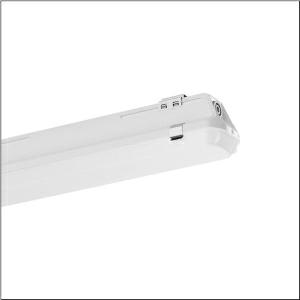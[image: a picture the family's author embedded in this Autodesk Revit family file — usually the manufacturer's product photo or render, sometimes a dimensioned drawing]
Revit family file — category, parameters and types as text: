
# Revit family: monsun_r__21_51fb10dp460b_c90e
name_source: partatom
category: Lighting Fixtures
units: mm (PartAtom-declared; Revit-internal decimal feet)

## family parameters
Cut with Voids When Loaded = No
Host = Face
Light Source = No
Part Type = Normal
Room Calculation Point = No
Round Connector Dimension = Use Diameter
Shared = No

## types (1)
- --- (1 x LED, 6060 lm, 39.4 W, 4000K)
    Apparent Load = 39 VA
    CIE Flux Codes = 47 77 93 94 100
    Color Rendering = 80
    Color Temperature = 4000K
    Default Elevation = 1800 mm
    Description = Monsun® 21, damp-proof luminaire, chain hanger, primary optical cover: enclosure, of PMMA, light emission: direct distribution, primary light characteristic: symmetric, installation type: suspended mounting, surface-mounted, horizontal mounting, vertical mounting, LED, rated luminous flux: 6.060lm, luminous efficacy: 154lm/W, light colour: 840, colour temperature: 4000K, control gear: ECG DALI, with terminal, 5-pole, max. 2.5mm², mains connection: 220..240V, AC, 50/60Hz, rated input power: 39W, housing, of glass-fibre reinforced polyester, uncoated, bright grey, incl. chain hanger, length: 1.590mm, width: 90mm, height: 88mm, clip for enclosure, of stainless steel (V2A), ceiling mounting element, of stainless steel (V2A), chain hanger, of stainless steel (V2A), protection rating (complete): IP66, insulation class (complete): insulation class I (protective earthing), certification: CE, ENEC, VDE, UKCA, protection symbol: D, impact resistance: IK04, permissible operating ambient temperature: -25..+35°C, standard: EN 50419, EN 60598-2-1, corresponds to IFS (International Featured Standards) requirements for safety and quality in the food industry, for indoor or canopied outdoor use, no direct snow, no direct sun, no direct rain, contact your sales advisor before using the luminaires in applications with unclear chemical exposure, large temperature fluctuations or condensation-forming humidity, LABS conformity tested according to VDMA 24364:2018-05, packaging unit: 1 piece
    Height = 89 mm
    Lamp = 1 x LED
    Lamp Light Flux = 6060 lm
    Lamp Power = 39.4 W
    Lamp count = 1
    Length = 1590 mm
    Luminous efficacy = 154 lm/W
    Manufacturer = Siteco
    ModVariant = No
    Model = 51FB10DP460B
    Mounting Place = Ceiling
    Mounting Type = Surface mounted
    Number of Poles = 1
    OnlyDefault = Yes
    Power Factor = 1
    Product Name = Monsun® 21
    Product group = damp-proof luminaire
    ProductGroupID = 300
    Protection Class = Protection class I
    Protection Degree = IP 66
    RLX_Detail_Level = 1
    RLX_Emergency_Light_Flux = 0 lm
    RLX_Emergency_Type = 0
    RLX_Emergency_Type_DB = No
    RlxData = <blob elided: 92121 chars, md5=8605f60a>
    Socket = socket
    Standby Power = 0 W
    System Light Flux = 6060 lm
    System Power = 39 W
    Type Comments = factory setting: luminous flux: 100 % | dim-lin: 254 | 261 mA
    Type Image = l_1006717.jpg
    URL = http://relux.com
    VarID = @adj_134507
    Voltage = 0 V
    Weight = 0.00 kg
    Width = 90 mm

## geometry (parser evidence)
native form markers: Blend x4, Sweep x13
no freeform markers — native parametric forms only
